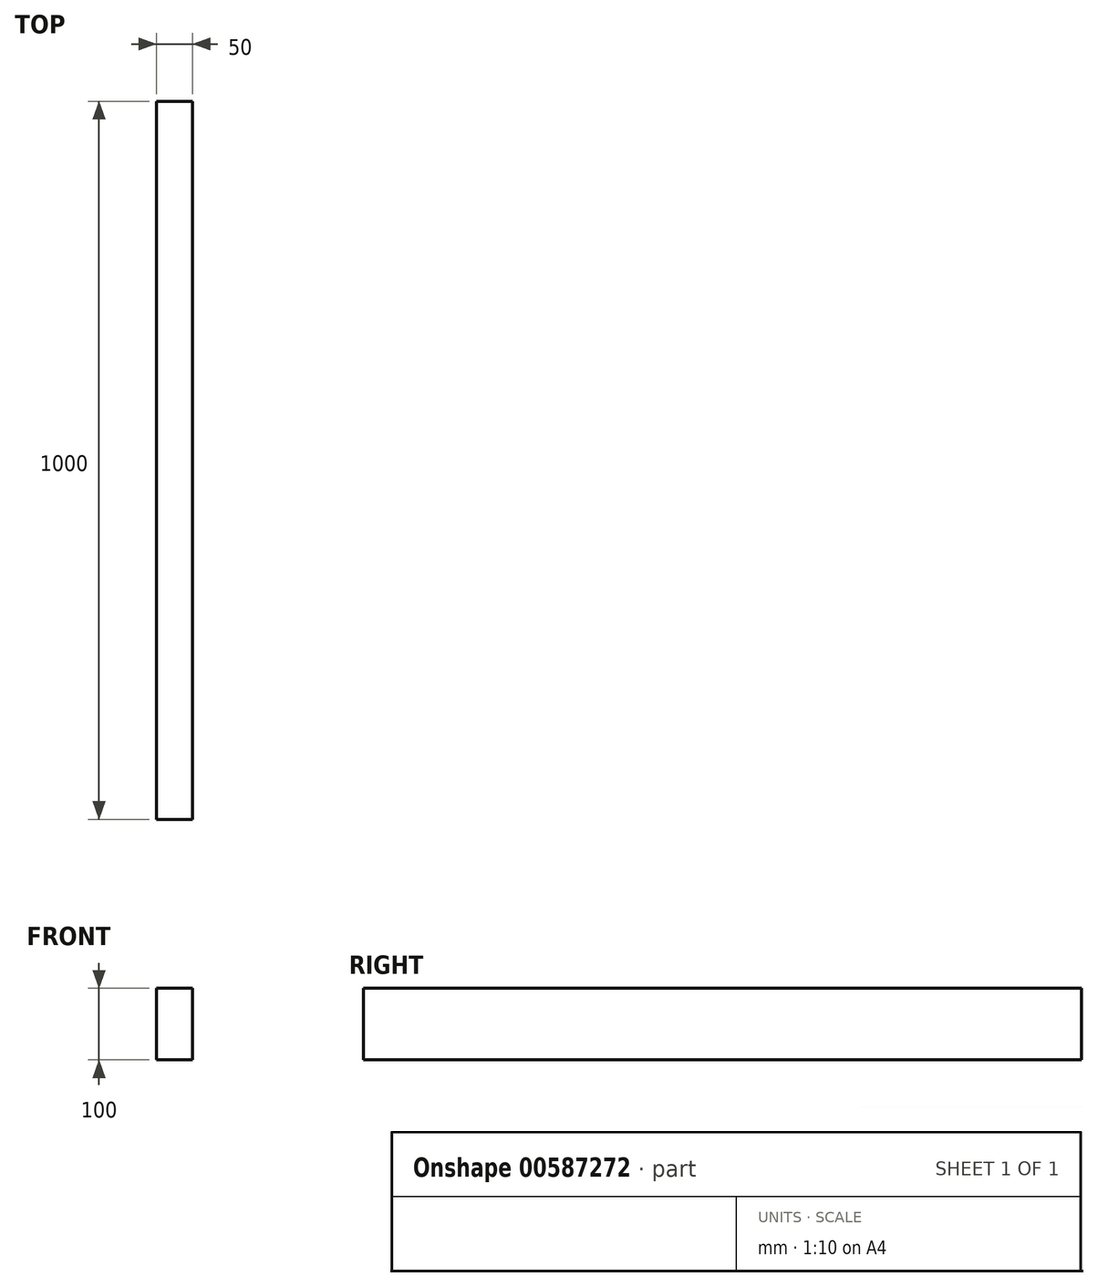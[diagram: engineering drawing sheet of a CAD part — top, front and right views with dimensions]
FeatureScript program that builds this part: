
annotation { "Feature Type Name" : "Feature", "Feature Type Description" : "" }
export const myFeature = defineFeature(function(context is Context, id is Id, definition is map)
    precondition{}
    {
        {
            var Q0;
            Q0=qCreatedBy(makeId("Front.planeOp"),FACE);
            var sketch = newSketch(context, id + "F0", { "sketchPlane" : qUnion([Q0])});
            skLineSegment(sketch, "E0.bottom", {"start": v(25, 50) * mm, "end": v(-25, 50) * mm});
            skLineSegment(sketch, "E0.top", {"start": v(25, -50) * mm, "end": v(-25, -50) * mm});
            skLineSegment(sketch, "E0.left", {"start": v(25, 50) * mm, "end": v(25, -50) * mm});
            skLineSegment(sketch, "E0.right", {"start": v(-25, 50) * mm, "end": v(-25, -50) * mm});
            skPoint(sketch, "E0.middle", {"position": v(0, 0) * mm});
            skSolve(sketch);
        }
        {
            var Q0;
            Q0=makeQuery(id+"F0.imprint","IMPRINT",FACE,{"disambiguationData":[TD([[makeQuery(id+"F0.imprint","IMPRINT",EDGE,{"derivedFrom":sQuery(id+"F0.wireOp",EDGE,"E0.bottom")}),1.0]])]});
            extrude(context, id + "F1", {"entities" : qUnion([Q0]), "endBound" : BoundingType.SYMMETRIC, "depth" : 1000 * mm, "offsetDistance" : 25.4 * mm});
        }
    });
